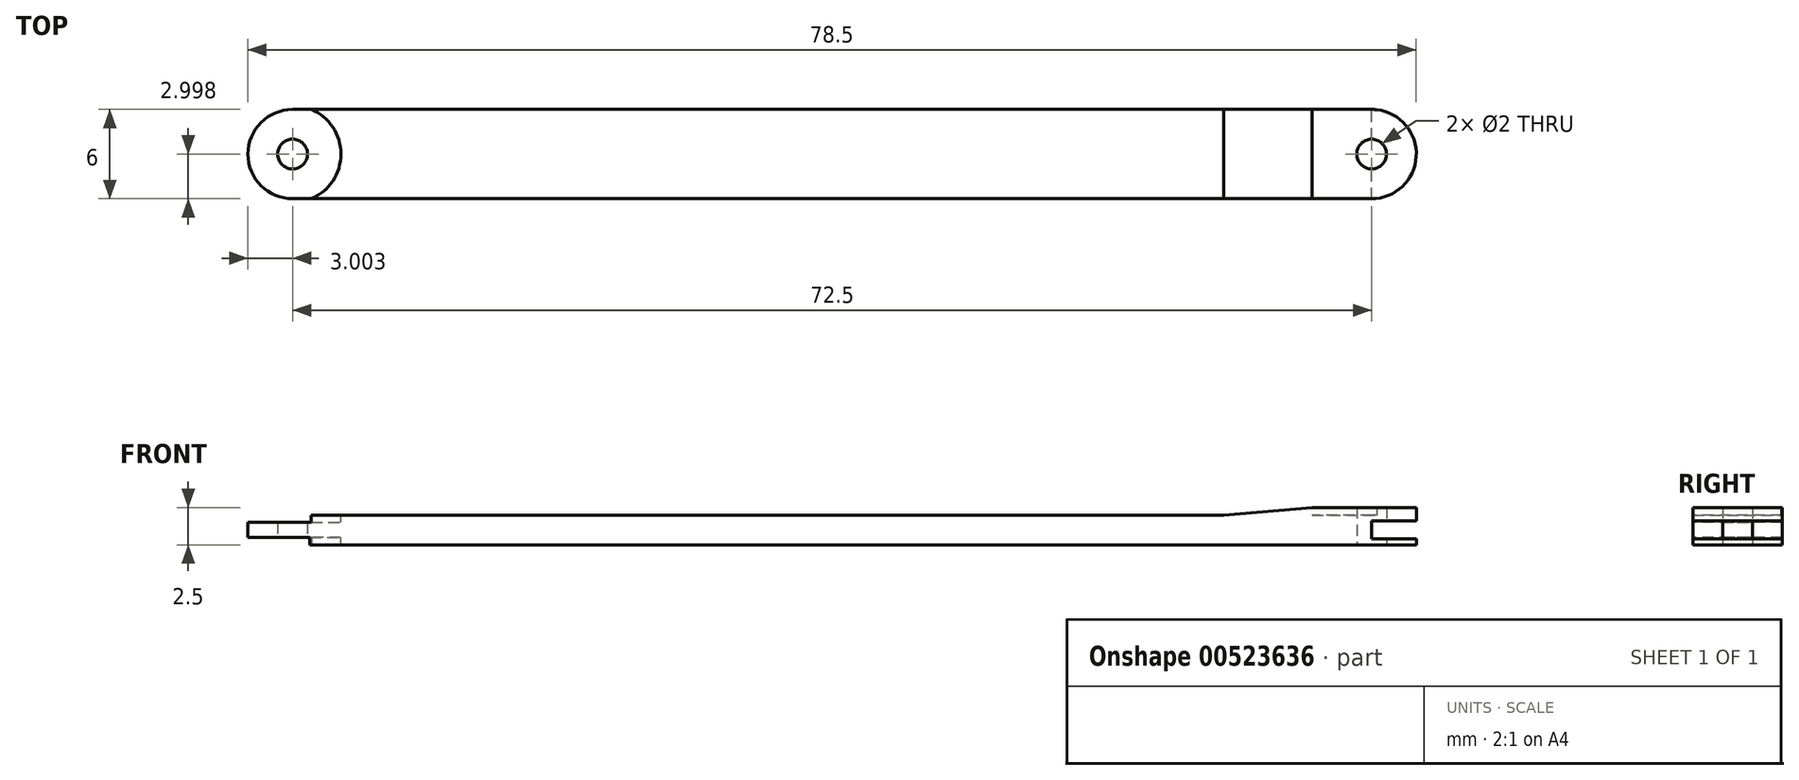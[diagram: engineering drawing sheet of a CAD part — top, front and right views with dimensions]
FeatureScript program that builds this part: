
annotation { "Feature Type Name" : "Feature", "Feature Type Description" : "" }
export const myFeature = defineFeature(function(context is Context, id is Id, definition is map)
    precondition{}
    {
        {
            var Q0;
            Q0=qCreatedBy(makeId("Top.planeOp"),FACE);
            var sketch = newSketch(context, id + "F0", { "sketchPlane" : qUnion([Q0])});
            skLineSegment(sketch, "E0.bottom", {"start": v(28.6, 5.22) * mm, "end": v(-43.9, 5.22) * mm});
            skLineSegment(sketch, "E0.top", {"start": v(28.6, 11.22) * mm, "end": v(-43.9, 11.22) * mm});
            skLineSegment(sketch, "E0.left", {"start": v(28.6, 5.22) * mm, "end": v(28.6, 11.22) * mm});
            skLineSegment(sketch, "E0.right", {"start": v(-43.9, 5.22) * mm, "end": v(-43.9, 11.22) * mm});
            skPoint(sketch, "E0.middle", {"position": v(-7.65, 8.22) * mm});
            skArc(sketch, "E1", {"start": v(28.6, 5.22) * mm, "mid": v(31.6, 8.22) * mm, "end": v(28.6, 11.22) * mm});
            skArc(sketch, "E2", {"start": v(-43.9, 11.22) * mm, "mid": v(-46.9, 8.22) * mm, "end": v(-43.9, 5.22) * mm});
            skPoint(sketch, "E3", {"position": v(-43.9, 11.22) * mm});
            skPoint(sketch, "E4", {"position": v(-43.9, 5.22) * mm});
            skSolve(sketch);
        }
        {
            var Q0;
            Q0 = qSketchRegion(id + "F0", true);
            extrude(context, id + "F1", {"entities" : qUnion([Q0]), "depth" : 2 * mm, "offsetDistance" : 25 * mm});
        }
        {
            var Q0;
            Q0=makeQuery(id+"F0.imprint","IMPRINT",FACE,{"disambiguationData":[TD([[makeQuery(id+"F0.imprint","IMPRINT",EDGE,{"derivedFrom":sQuery(id+"F0.wireOp",EDGE,"E0.bottom")}),-1.0]])]});
            var sketch = newSketch(context, id + "F2", { "sketchPlane" : qUnion([Q0])});
            skCircle(sketch, "E5", {"center": v(-43.92, 8.24) * mm, "radius": 3.25 * mm});
            skSolve(sketch);
        }
        {
            var Q0;
            Q0=makeQuery(id+"F1.opExtrude","CAP_FACE",FACE,{"disambiguationData":[OSD([sQuery(id+"F0.wireOp",EDGE,"E0.bottom"),sQuery(id+"F0.wireOp",EDGE,"E0.top"),sQuery(id+"F0.wireOp",EDGE,"E1"),sQuery(id+"F0.wireOp",EDGE,"E2")])],"isStart":false});
            var sketch = newSketch(context, id + "F3", { "sketchPlane" : qUnion([Q0])});
            skCircle(sketch, "E6", {"center": v(-43.9, 8.22) * mm, "radius": 3.25 * mm});
            skSolve(sketch);
        }
        {
            var Q0;
            {var subQ5=makeQuery(id+"F0.imprint","IMPRINT",EDGE,{"derivedFrom":sQuery(id+"F0.wireOp",EDGE,"E0.right")});Q0=makeQuery(id+"F2.imprint","IMPRINT",FACE,{"disambiguationData":[TD([[makeQuery(id+"F2.imprint","IMPRINT",EDGE,{"derivedFrom":subQ5}),1.0]])]});}
            var Q1;
            {var subQ5=makeQuery(id+"F0.imprint","IMPRINT",EDGE,{"derivedFrom":sQuery(id+"F0.wireOp",EDGE,"E0.right")});Q1=makeQuery(id+"F2.imprint","IMPRINT",FACE,{"disambiguationData":[TD([[makeQuery(id+"F2.imprint","IMPRINT",EDGE,{"derivedFrom":subQ5}),-1.0]])]});}
            extrude(context, id + "F4", {"entities" : qUnion([Q0, Q1]), "operationType" : NewBodyOperationType.REMOVE, "depth" : 0.5 * mm, "offsetDistance" : 25 * mm});
        }
        {
            var Q0;
            Q0=sQuery(id+"F0.wireOp",VERTEX,"E1.center");
            var Q1;
            Q1=makeQuery(id+"F1.opExtrude","SWEPT_BODY",BODY,{"disambiguationData":[OSD([sQuery(id+"F0.wireOp",EDGE,"E0.bottom"),sQuery(id+"F0.wireOp",EDGE,"E0.top"),sQuery(id+"F0.wireOp",EDGE,"E1"),sQuery(id+"F0.wireOp",EDGE,"E2")])]});
            hole(context, id + "F5", {"style" : HoleStyle.SIMPLE, "endStyle" : HoleEndStyle.BLIND, "oppositeDirection" : true, "holeDiameter" : 2 * mm, "holeDepth" : 6 * mm, "isTappedThrough" : true, "tappedDepth" : 12 * mm, "tapClearance" : 3, "startFromSketch" : true, "locations" : qUnion([Q0]), "scope" : qUnion([Q1])});
        }
        {
            var Q0;
            Q0=sQuery(id+"F0.wireOp",VERTEX,"E2.center");
            var Q1;
            Q1=makeQuery(id+"F1.opExtrude","SWEPT_BODY",BODY,{"disambiguationData":[OSD([sQuery(id+"F0.wireOp",EDGE,"E0.bottom"),sQuery(id+"F0.wireOp",EDGE,"E0.top"),sQuery(id+"F0.wireOp",EDGE,"E1"),sQuery(id+"F0.wireOp",EDGE,"E2")])]});
            hole(context, id + "F6", {"style" : HoleStyle.SIMPLE, "endStyle" : HoleEndStyle.BLIND, "oppositeDirection" : true, "holeDiameter" : 2 * mm, "holeDepth" : 6 * mm, "isTappedThrough" : true, "tappedDepth" : 12 * mm, "tapClearance" : 3, "startFromSketch" : true, "locations" : qUnion([Q0]), "scope" : qUnion([Q1])});
        }
        {
            var Q0;
            Q0 = qSketchRegion(id + "F3", true);
            extrude(context, id + "F7", {"entities" : qUnion([Q0]), "operationType" : NewBodyOperationType.REMOVE, "oppositeDirection" : true, "depth" : 0.5 * mm, "offsetDistance" : 25 * mm});
        }
        {
            var Q0;
            Q0=makeQuery(id+"F1.opExtrude","SWEPT_FACE",FACE,{"disambiguationData":[OSD([sQuery(id+"F0.wireOp",EDGE,"E0.top")])]});
            var sketch = newSketch(context, id + "F8", { "sketchPlane" : qUnion([Q0])});
            skLineSegment(sketch, "E7", {"start": v(-28.6, 0) * mm, "end": v(-24.6, 0) * mm});
            skLineSegment(sketch, "E8", {"start": v(-24.6, 0) * mm, "end": v(-24.6, 2) * mm});
            skLineSegment(sketch, "E9", {"start": v(-24.6, 2) * mm, "end": v(-24.6, 1.6) * mm});
            skLineSegment(sketch, "E10", {"start": v(-24.6, 0) * mm, "end": v(-24.6, 0.4) * mm});
            skLineSegment(sketch, "E11.bottom", {"start": v(-24.6, 0.4) * mm, "end": v(-33.34, 0.4) * mm});
            skLineSegment(sketch, "E11.top", {"start": v(-24.6, 1.6) * mm, "end": v(-33.34, 1.6) * mm});
            skLineSegment(sketch, "E11.left", {"start": v(-24.6, 0.4) * mm, "end": v(-24.6, 1.6) * mm});
            skLineSegment(sketch, "E11.right", {"start": v(-33.34, 0.4) * mm, "end": v(-33.34, 1.6) * mm});
            skSolve(sketch);
        }
        {
            var Q0;
            {var subQ0=sQuery(id+"F8.wireOp",EDGE,"E11.left");Q0=makeQuery(id+"F8.imprint","IMPRINT",FACE,{"disambiguationData":[TD([[makeQuery(id+"F8.imprint","IMPRINT",EDGE,{"derivedFrom":subQ0}),1.0]])]});}
            var Q1;
            {var subQ0=sQuery(id+"F8.wireOp",EDGE,"E11.right");Q1=makeQuery(id+"F8.imprint","IMPRINT",FACE,{"disambiguationData":[TD([[makeQuery(id+"F8.imprint","IMPRINT",EDGE,{"derivedFrom":subQ0}),-1.0]])]});}
            extrude(context, id + "F9", {"entities" : qUnion([Q0, Q1]), "operationType" : NewBodyOperationType.REMOVE, "oppositeDirection" : true, "depth" : 25 * mm, "offsetDistance" : 25 * mm});
        }
        {
            var Q0;
            Q0=makeQuery(id+"F1.opExtrude","CAP_FACE",FACE,{"disambiguationData":[OSD([sQuery(id+"F0.wireOp",EDGE,"E0.bottom"),sQuery(id+"F0.wireOp",EDGE,"E0.top"),sQuery(id+"F0.wireOp",EDGE,"E1"),sQuery(id+"F0.wireOp",EDGE,"E2")])],"isStart":false});
            var sketch = newSketch(context, id + "F10", { "sketchPlane" : qUnion([Q0])});
            skLineSegment(sketch, "E12", {"start": v(28.6, 5.22) * mm, "end": v(24.6, 5.22) * mm});
            skLineSegment(sketch, "E13", {"start": v(24.6, 5.22) * mm, "end": v(24.6, 11.22) * mm});
            skLineSegment(sketch, "E14", {"start": v(24.6, 11.22) * mm, "end": v(28.95, 11.2) * mm});
            skSolve(sketch);
        }
        {
            var Q0;
            Q0 = qSketchRegion(id + "F10", true);
            var Q1;
            {var subQ2=sQuery(id+"F10.wireOp",EDGE,"E12");Q1=makeQuery(id+"F10.imprint","IMPRINT",FACE,{"disambiguationData":[TD([[makeQuery(id+"F10.imprint","IMPRINT",EDGE,{"derivedFrom":subQ2}),-1.0]])]});}
            extrude(context, id + "F11", {"entities" : qUnion([Q0, Q1]), "operationType" : NewBodyOperationType.ADD, "depth" : 0.5 * mm, "offsetDistance" : 25 * mm});
        }
        {
            var Q0;
            Q0=makeQuery(id+"F11.boolean.opBoolean","MERGE",FACE,{"derivedFrom":[makeQuery(id+"F1.opExtrude","SWEPT_FACE",FACE,{"disambiguationData":[OSD([sQuery(id+"F0.wireOp",EDGE,"E0.bottom")])]}),makeQuery(id+"F11.opExtrude","SWEPT_FACE",FACE,{"disambiguationData":[OSD([sQuery(id+"F10.wireOp",EDGE,"E12")])]})]});
            var sketch = newSketch(context, id + "F12", { "sketchPlane" : qUnion([Q0])});
            skLineSegment(sketch, "E15", {"start": v(24.6, 2.5) * mm, "end": v(18.65, 2) * mm});
            skLineSegment(sketch, "E16", {"start": v(18.65, 2) * mm, "end": v(24.6, 2) * mm});
            skLineSegment(sketch, "E17", {"start": v(24.6, 2) * mm, "end": v(24.6, 2.5) * mm});
            skSolve(sketch);
        }
        {
            var Q0;
            Q0=makeQuery(id+"F12.imprint","IMPRINT",FACE,{"disambiguationData":[TD([[makeQuery(id+"F12.imprint","IMPRINT",EDGE,{"derivedFrom":sQuery(id+"F12.wireOp",EDGE,"E15")}),1.0]])]});
            extrude(context, id + "F13", {"entities" : qUnion([Q0]), "operationType" : NewBodyOperationType.ADD, "oppositeDirection" : true, "depth" : 6 * mm, "offsetDistance" : 25 * mm});
        }
    });
